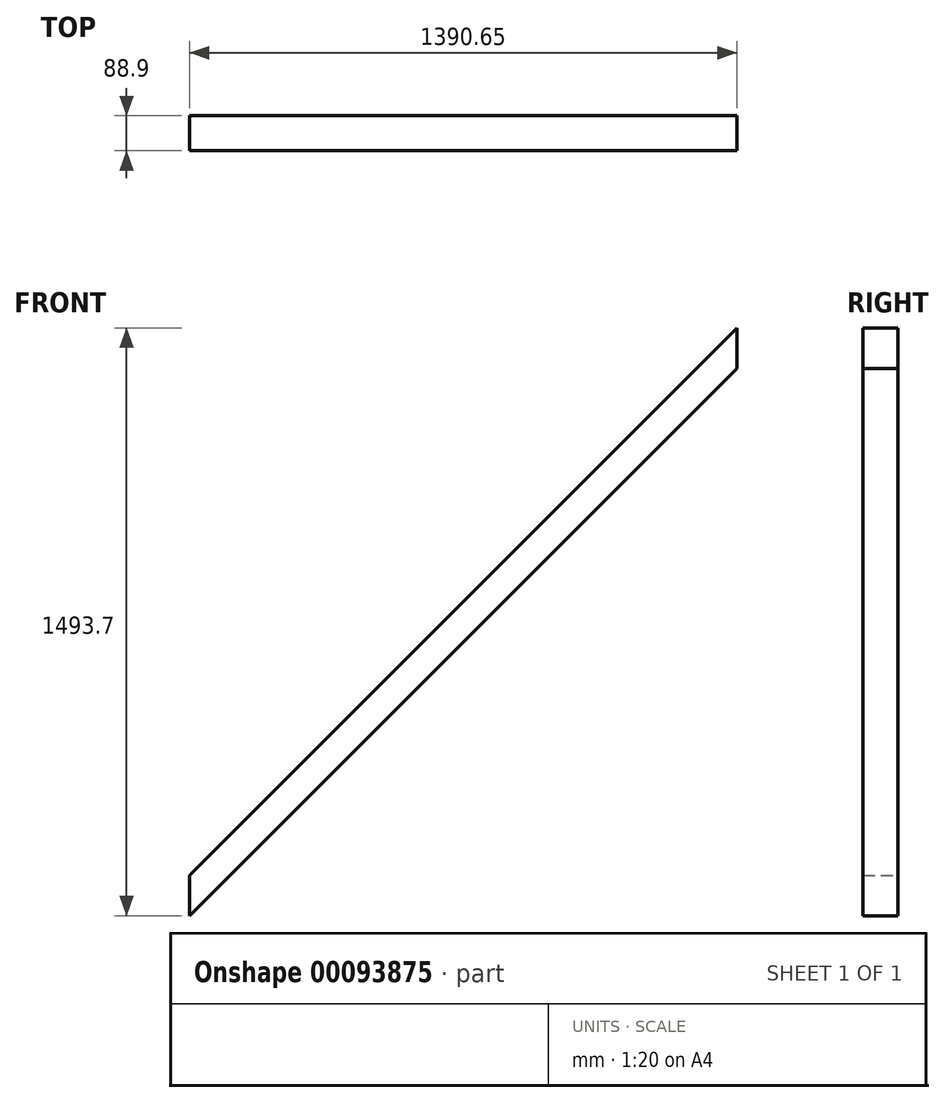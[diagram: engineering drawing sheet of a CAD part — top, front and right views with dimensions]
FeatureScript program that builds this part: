
annotation { "Feature Type Name" : "Feature", "Feature Type Description" : "" }
export const myFeature = defineFeature(function(context is Context, id is Id, definition is map)
    precondition{}
    {
        {
            var Q0;
            Q0=qCreatedBy(makeId("Front.planeOp"),FACE);
            var sketch = newSketch(context, id + "F0", { "sketchPlane" : qUnion([Q0])});
            skLineSegment(sketch, "E0", {"start": v(0, 0) * mm, "end": v(0, 103.05) * mm});
            skLineSegment(sketch, "E1", {"start": v(0, 103.05) * mm, "end": v(-1390.65, -1287.6) * mm});
            skLineSegment(sketch, "E2", {"start": v(-1390.65, -1287.6) * mm, "end": v(-1390.65, -1390.65) * mm});
            skLineSegment(sketch, "E3", {"start": v(-1390.65, -1390.65) * mm, "end": v(0, 0) * mm});
            skSolve(sketch);
        }
        {
            var Q0;
            Q0 = qSketchRegion(id + "F0", true);
            extrude(context, id + "F1", {"entities" : qUnion([Q0]), "depth" : 88.9 * mm, "offsetDistance" : 25.4 * mm});
        }
    });
